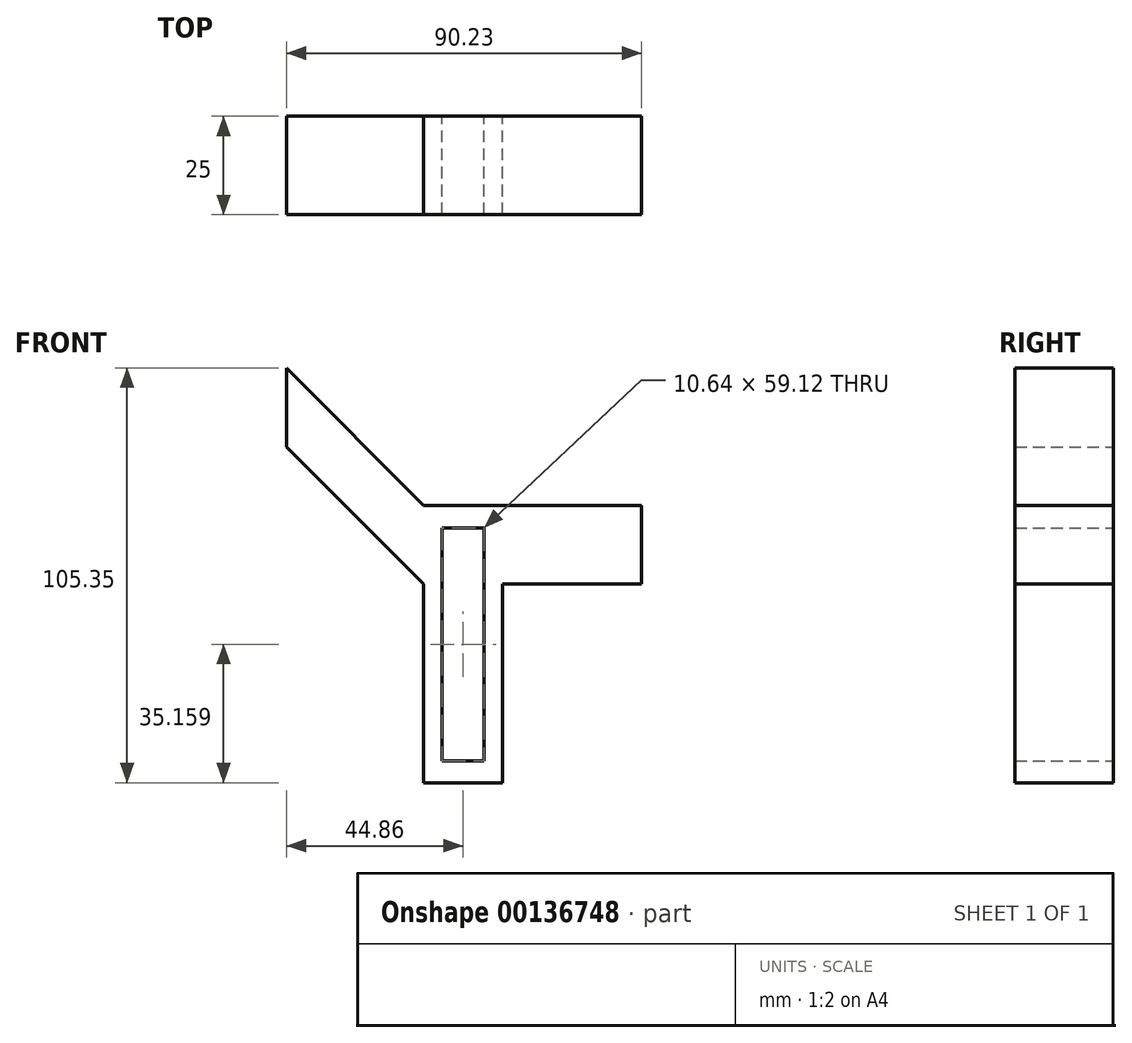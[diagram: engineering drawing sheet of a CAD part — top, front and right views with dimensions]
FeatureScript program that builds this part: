
annotation { "Feature Type Name" : "Feature", "Feature Type Description" : "" }
export const myFeature = defineFeature(function(context is Context, id is Id, definition is map)
    precondition{}
    {
        {
            var Q0;
            Q0=qCreatedBy(makeId("Front.planeOp"),FACE);
            var sketch = newSketch(context, id + "F0", { "sketchPlane" : qUnion([Q0])});
            skLineSegment(sketch, "E0", {"start": v(0, 0) * mm, "end": v(20, 0) * mm});
            skLineSegment(sketch, "E1", {"start": v(20, 0) * mm, "end": v(20, 50.5) * mm});
            skLineSegment(sketch, "E2", {"start": v(20, 50.5) * mm, "end": v(55.37, 50.5) * mm});
            skLineSegment(sketch, "E3", {"start": v(55.37, 50.5) * mm, "end": v(55.37, 70.5) * mm});
            skLineSegment(sketch, "E4", {"start": v(55.37, 70.5) * mm, "end": v(0, 70.5) * mm});
            skLineSegment(sketch, "E5", {"start": v(0, 70.5) * mm, "end": v(-34.86, 105.35) * mm});
            skLineSegment(sketch, "E6", {"start": v(-34.86, 105.35) * mm, "end": v(-34.86, 85.35) * mm});
            skLineSegment(sketch, "E7", {"start": v(-34.86, 85.35) * mm, "end": v(0, 50.5) * mm});
            skLineSegment(sketch, "E8", {"start": v(0, 50.5) * mm, "end": v(0, 0) * mm});
            skPoint(sketch, "E9.centerSnap0", {"position": v(10, 0) * mm});
            skLineSegment(sketch, "E10.bottom", {"start": v(15.32, 5.6) * mm, "end": v(4.68, 5.6) * mm});
            skLineSegment(sketch, "E10.top", {"start": v(15.32, 64.72) * mm, "end": v(4.68, 64.72) * mm});
            skLineSegment(sketch, "E10.left", {"start": v(15.32, 5.6) * mm, "end": v(15.32, 64.72) * mm});
            skLineSegment(sketch, "E10.right", {"start": v(4.68, 5.6) * mm, "end": v(4.68, 64.72) * mm});
            skPoint(sketch, "E10.middle", {"position": v(10, 35.16) * mm});
            skSolve(sketch);
        }
        {
            var Q0;
            Q0=makeQuery(id+"F0.imprint","IMPRINT",FACE,{"disambiguationData":[TD([[makeQuery(id+"F0.imprint","IMPRINT",EDGE,{"derivedFrom":sQuery(id+"F0.wireOp",EDGE,"E0")}),1.0]])]});
            extrude(context, id + "F1", {"entities" : qUnion([Q0]), "depth" : 25 * mm, "offsetDistance" : 25 * mm});
        }
    });
